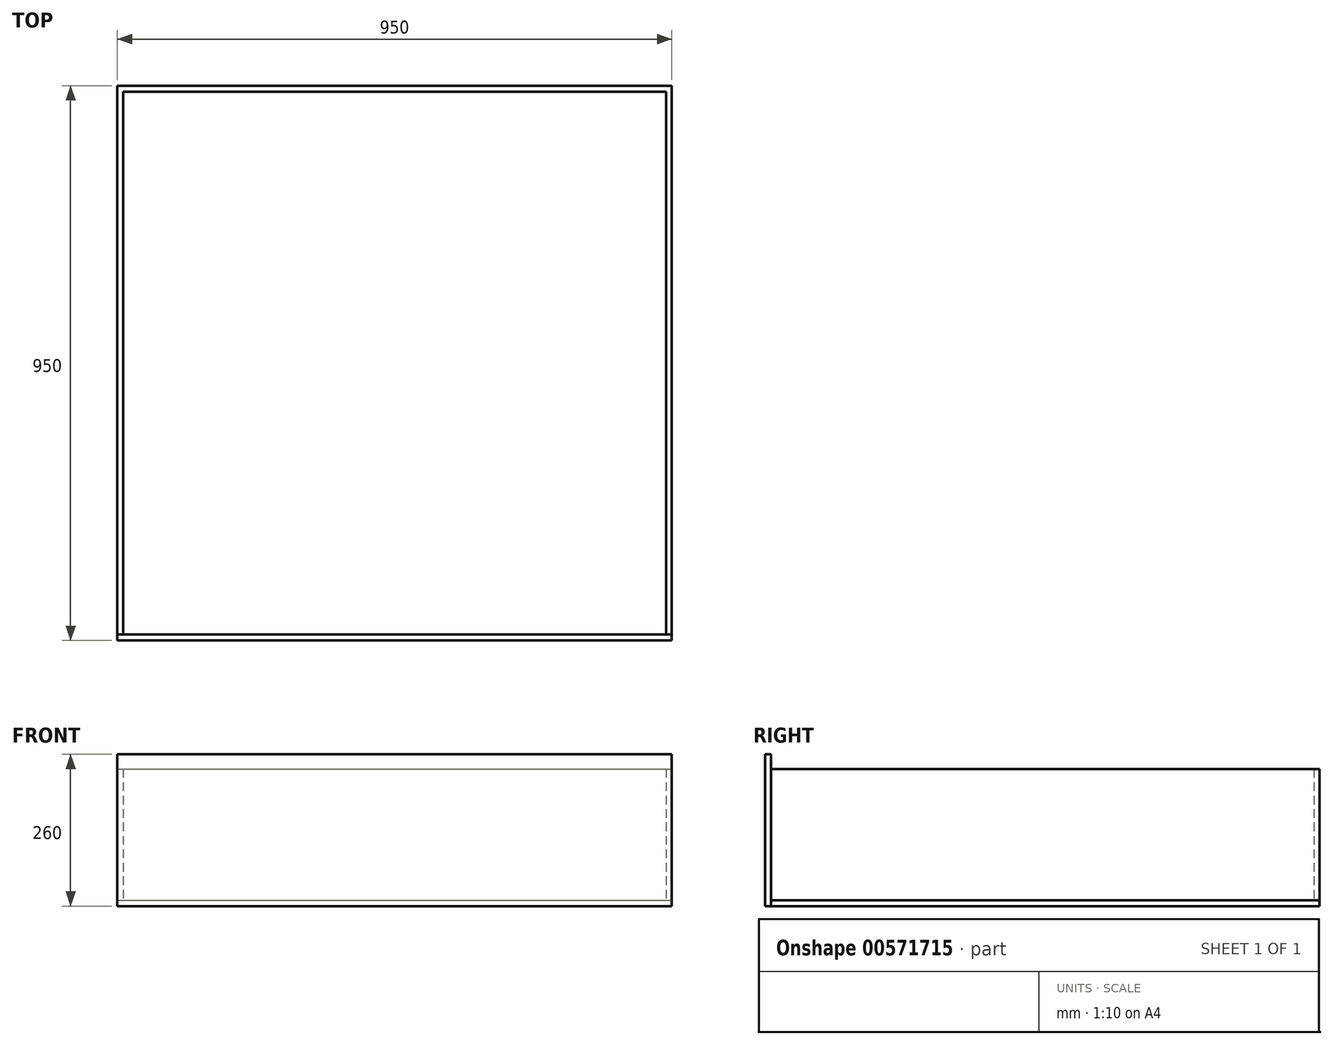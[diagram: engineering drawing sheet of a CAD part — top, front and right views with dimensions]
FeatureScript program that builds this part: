
annotation { "Feature Type Name" : "Feature", "Feature Type Description" : "" }
export const myFeature = defineFeature(function(context is Context, id is Id, definition is map)
    precondition{}
    {
        {
            var Q0;
            Q0=qCreatedBy(makeId("Top.planeOp"),FACE);
            var sketch = newSketch(context, id + "F0", { "sketchPlane" : qUnion([Q0])});
            skLineSegment(sketch, "E0.bottom", {"start": v(0, 0) * mm, "end": v(950, 0) * mm});
            skLineSegment(sketch, "E0.top", {"start": v(0, 940) * mm, "end": v(950, 940) * mm});
            skLineSegment(sketch, "E0.left", {"start": v(0, 0) * mm, "end": v(0, 940) * mm});
            skLineSegment(sketch, "E0.right", {"start": v(950, 0) * mm, "end": v(950, 940) * mm});
            skSolve(sketch);
        }
        {
            var Q0;
            Q0 = qSketchRegion(id + "F0", true);
            extrude(context, id + "F1", {"entities" : qUnion([Q0]), "depth" : 10 * mm, "offsetDistance" : 25 * mm});
        }
        {
            var Q0;
            Q0=makeQuery(id+"F1.opExtrude","CAP_FACE",FACE,{"disambiguationData":[OSD([sQuery(id+"F0.wireOp",EDGE,"E0.bottom"),sQuery(id+"F0.wireOp",EDGE,"E0.top"),sQuery(id+"F0.wireOp",EDGE,"E0.left"),sQuery(id+"F0.wireOp",EDGE,"E0.right")])],"isStart":false});
            var sketch = newSketch(context, id + "F2", { "sketchPlane" : qUnion([Q0])});
            skLineSegment(sketch, "E1.bottom", {"start": v(0, 940) * mm, "end": v(950, 940) * mm});
            skLineSegment(sketch, "E1.top", {"start": v(0, 930) * mm, "end": v(950, 930) * mm});
            skLineSegment(sketch, "E1.left", {"start": v(0, 940) * mm, "end": v(0, 930) * mm});
            skLineSegment(sketch, "E1.right", {"start": v(950, 940) * mm, "end": v(950, 930) * mm});
            skLineSegment(sketch, "E2.bottom", {"start": v(0, 930) * mm, "end": v(10, 930) * mm});
            skLineSegment(sketch, "E2.top", {"start": v(0, 0) * mm, "end": v(10, 0) * mm});
            skLineSegment(sketch, "E2.left", {"start": v(0, 930) * mm, "end": v(0, 0) * mm});
            skLineSegment(sketch, "E2.right", {"start": v(10, 930) * mm, "end": v(10, 0) * mm});
            skLineSegment(sketch, "E3.bottom", {"start": v(950, 930) * mm, "end": v(940, 930) * mm});
            skLineSegment(sketch, "E3.top", {"start": v(950, 0) * mm, "end": v(940, 0) * mm});
            skLineSegment(sketch, "E3.left", {"start": v(950, 930) * mm, "end": v(950, 0) * mm});
            skLineSegment(sketch, "E3.right", {"start": v(940, 930) * mm, "end": v(940, 0) * mm});
            skSolve(sketch);
        }
        {
            var Q0;
            Q0 = qSketchRegion(id + "F2", true);
            extrude(context, id + "F3", {"entities" : qUnion([Q0]), "depth" : 225 * mm, "offsetDistance" : 25 * mm});
        }
        {
            var Q0;
            Q0=makeQuery(id+"F1.opExtrude","SWEPT_FACE",FACE,{"disambiguationData":[OSD([sQuery(id+"F0.wireOp",EDGE,"E0.bottom")])]});
            var sketch = newSketch(context, id + "F4", { "sketchPlane" : qUnion([Q0])});
            skLineSegment(sketch, "E4.bottom", {"start": v(0, 0) * mm, "end": v(950, 0) * mm});
            skLineSegment(sketch, "E4.top", {"start": v(0, 260) * mm, "end": v(950, 260) * mm});
            skLineSegment(sketch, "E4.left", {"start": v(0, 0) * mm, "end": v(0, 260) * mm});
            skLineSegment(sketch, "E4.right", {"start": v(950, 0) * mm, "end": v(950, 260) * mm});
            skSolve(sketch);
        }
        {
            var Q0;
            Q0 = qSketchRegion(id + "F4", true);
            extrude(context, id + "F5", {"entities" : qUnion([Q0]), "depth" : 10 * mm, "offsetDistance" : 25 * mm});
        }
    });
